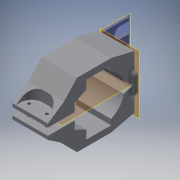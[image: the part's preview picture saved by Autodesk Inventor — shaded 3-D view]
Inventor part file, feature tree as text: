
AUTODESK INVENTOR PART (.ipt)
format: ipt  version: 2016 (Build 200138000, 138)  size: 445,952 bytes
history: native  units: in
note: dims shown in document units (in); Inventor stores cm internally (conversion verified against a paired STEP export)
features: sketch x12, extrude x11, projected_geometry x6, plane x4, reference x4, fillet x3, revolve x1
ambient origin geometry x8: Origin, YZ Plane, XZ Plane, XY Plane, X Axis, Y Axis, Z Axis, Center Point
bodies: Solid1 (feature_tree)
feature tree (41):
  plane  "Work Plane1"
  plane  "Work Plane2"
  extrude  "Extrusion1"  Depth=1.315in
  plane  "Work Plane3"
  extrude  "Extrusion2"  Depth=1.4in
  extrude  "Extrusion3"  Depth=1.8in TaperAngle=0.0deg
  plane  "Work Plane4"
  revolve  "Revolution1"  [1 undecoded]
  fillet  "Fillet1"  Radius=1.925in
  extrude  "Extrusion4"  TaperAngle=90.0deg  [1 undecoded]
  extrude  "Extrusion5"  Depth=0.2in TaperAngle=0.0deg
  extrude  "Extrusion6"  Depth=0.2in TaperAngle=0.0deg
  extrude  "Extrusion7"  Depth=2.575in TaperAngle=0.0deg
  extrude  "Extrusion8"  Depth=0.175in
  extrude  "Extrusion9"  Depth=0.2in TaperAngle=0.0deg
  fillet  "Fillet2"  Radius=0.2in
  fillet  "Fillet3"  Radius=0.625in
  extrude  "Extrusion10"  Depth=0.35in
  extrude  "Extrusion11"  Depth=0.2in
  sketch  "Sketch1"  dims[d2=0.6575in d3=1.315in]
  reference  "Reference1"
  sketch  "Sketch2"  dims[d10=2.92in d11=1.4in]
  sketch  "Sketch3"  dims[d12=0.35in d13=1.8in d14=0.0in]
  reference  "Reference2"
  sketch  "Sketch4"  dims[d15=0.5in d16=0.35in d17=1.925in d18=0.0in]
  reference  "Reference3"
  sketch  "Sketch5"  dims[d19=1.925in d20=0.0in d21=90.0deg]
  projected_geometry  "Projected Loop1"
  reference  "Reference4"
  sketch  "Sketch6"  dims[d22=0.3125in d23=0.2in d24=0.0in]
  projected_geometry  "Projected Loop2"
  sketch  "Sketch7"  dims[d25=1.5in d26=0.2in d27=0.0in]
  projected_geometry  "Projected Loop3"
  sketch  "Sketch8"  dims[d28=0.4in d29=2.575in d30=0.0in]
  projected_geometry  "Projected Loop4"
  sketch  "Sketch9"  dims[d31=0.175in d32=0.175in]
  sketch  "Sketch10"  dims[d33=2.575in d34=0.0in d35=0.2in d36=0.0in d37=0.2in d38=0.0in d39=0.625in]
  sketch  "Sketch11"  dims[d40=0.625in d41=0.35in]
  projected_geometry  "Projected Loop5"
  sketch  "Sketch12"  dims[d44=0.3in d45=0.2in d46=0.2in d47=0.4in d48=90.0deg d49=0.3in d50=10.0in d51=0.0in d52=0.2in d53=0.0in]
  projected_geometry  "Projected Loop6"
note: 2 required parameter values undecoded (feature->parameter linkage not recoverable at this tier; creation-order binding heuristic only, values carry confidence <= 0.55)